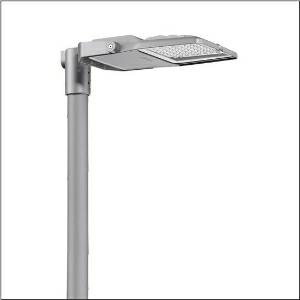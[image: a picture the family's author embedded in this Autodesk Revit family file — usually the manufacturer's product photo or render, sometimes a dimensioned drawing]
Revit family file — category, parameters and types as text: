
# Revit family: floodlight_fl_21_iq_mini___pl61_5xa7771d4c3a_f55b
name_source: partatom
category: Lighting Fixtures
units: mm (PartAtom-declared; Revit-internal decimal feet)

## family parameters
Cut with Voids When Loaded = No
Host = Face
Light Source = No
Part Type = Normal
Room Calculation Point = No
Round Connector Dimension = Use Diameter
Shared = No

## types (1)
- --- (1 x LED, 18260 lm, 143 W, 4000K)
    Apparent Load = 143 VA
    CIE Flux Codes = 33 65 98 100 100
    Color Rendering = 70
    Color Temperature = 4000K
    Default Elevation = 1800 mm
    Description = Floodlight FL 21 iQ mini, floodlight, primary light control with lens, of PMMA, primary optical cover: protective disc, of toughened safety glass, transparent, light distribution: PL61, light emission: direct distribution, installation type: surface-mounted, LED, High Power LED, rated luminous flux: 18.260lm, luminous efficacy: 128lm/W, light colour: 740, colour temperature: 4000K, control gear: iQ Comfort/DALI, control: Auto-Match, Temp-Guard, Lumen-Switch, Night-Set, Smart-Wire, Light-Fading, Desk-Remote (wireless, voltage-free reading and setting of iQ features in the workshop via application-optimized NFC function/RFID function), optimised constant luminous flux control (CLO 2.0), with terminal, 6-pole, mains connection: 220..240V, AC, 50/60Hz, start of lifetime: 143W, end of service life: 152W, reduction: 61W, luminaire housing, of diecast aluminium, powder-coated, Siteco® metallic grey (DB 702S), corrosivity category C5 mid according to DIN EN ISO 12944, suitable for swimming pools, chlorine-resistant, sealing non-destructively replaceable, please order mast flange separately, mast bracket, of steel, galvanised, powder-coated, Siteco® metallic grey (DB 702S), protection rating (complete): IP66, insulation class (complete): insulation class II (safety insulation), certification: CE, ENEC, VDE, protection symbol: D, impact resistance: IK08, permissible operating ambient temperature: -40..+40°C, permissible operating ambient temperature for outdoor applications: -40..+50°C, standard: DIN EN 12944, LABS conformity tested according to VDMA 24364:2018-05, packaging unit: 1 piece

Light Distribution: PL61
    Height = 70 mm
    Lamp = 1 x LED
    Lamp Light Flux = 18260 lm
    Lamp Power = 143 W
    Lamp count = 1
    Length = 485 mm
    Luminous efficacy = 128 lm/W
    Manufacturer = Siteco
    ModVariant = No
    Model = 5XA7771D4C3A
    Number of Poles = 1
    OnlyDefault = Yes
    Power Factor = 1
    Product Name = Floodlight FL 21 iQ mini | PL61
    Product group = floodlight | pylon annexe
    ProductGroupID = 6200
    Protection Class = Protection class II
    Protection Degree = IP 66
    RLX_Detail_Level = 1
    RLX_Emergency_Light_Flux = 0 lm
    RLX_Emergency_Type = 0
    RLX_Emergency_Type_DB = No
    RlxData = <blob elided: 101665 chars, md5=49d33e58>
    Socket = socket
    Standby Power = 0 W
    System Light Flux = 18260 lm
    System Power = 143 W
    Type Comments = factory setting: luminous flux: 100 % | dim-lin: 254 | 730 mA
    Type Image = l_1007125.jpg
    URL = http://relux.com
    VarID = @adj_172604
    Voltage = 0 V
    Weight = 0.00 kg
    Width = 337 mm

## geometry (parser evidence)
native form markers: Blend x4, Sweep x12
no freeform markers — native parametric forms only
